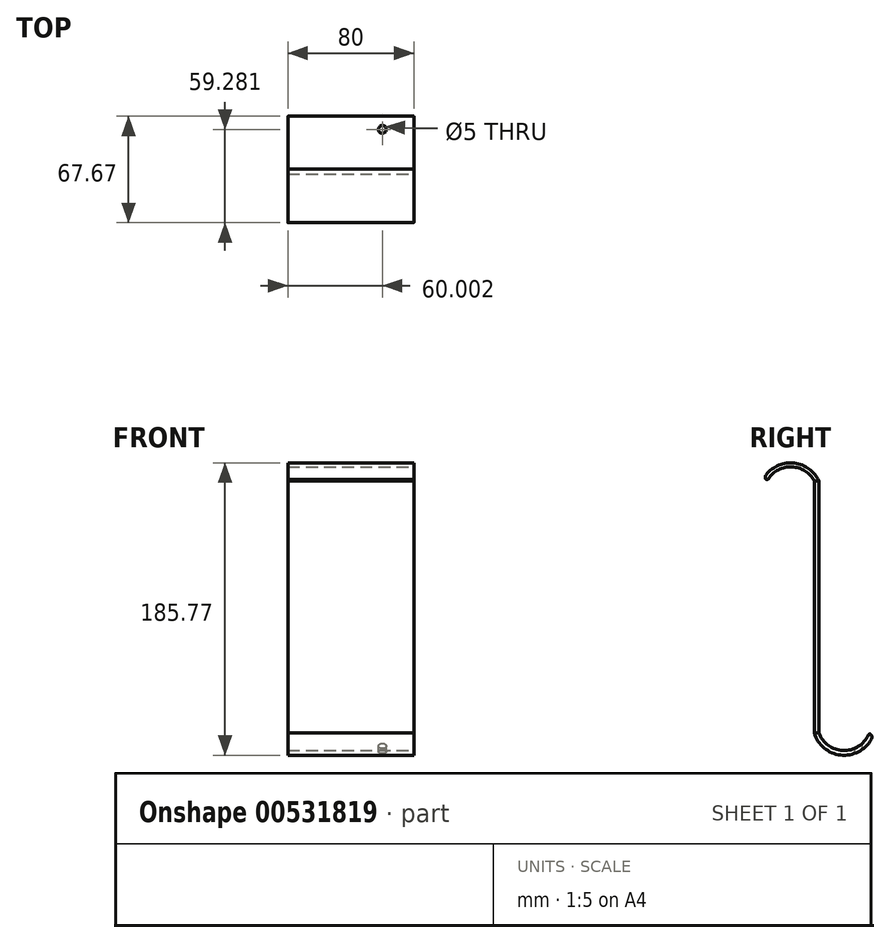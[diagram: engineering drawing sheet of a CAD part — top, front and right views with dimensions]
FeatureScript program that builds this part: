
annotation { "Feature Type Name" : "Feature", "Feature Type Description" : "" }
export const myFeature = defineFeature(function(context is Context, id is Id, definition is map)
    precondition{}
    {
        {
            var Q0;
            Q0=qCreatedBy(makeId("Front.planeOp"),FACE);
            var sketch = newSketch(context, id + "F0", { "sketchPlane" : qUnion([Q0])});
            skLineSegment(sketch, "E0", {"start": v(-47.36, 34.9) * mm, "end": v(32.64, 34.9) * mm});
            skLineSegment(sketch, "E1", {"start": v(-47.36, 34.9) * mm, "end": v(-47.36, -125.1) * mm});
            skLineSegment(sketch, "E2", {"start": v(-47.36, -125.1) * mm, "end": v(32.64, -125.1) * mm});
            skLineSegment(sketch, "E3", {"start": v(32.64, -125.1) * mm, "end": v(32.64, 34.9) * mm});
            skSolve(sketch);
        }
        {
            var Q0;
            Q0=makeQuery(id+"F0.imprint","IMPRINT",FACE,{"disambiguationData":[TD([[makeQuery(id+"F0.imprint","IMPRINT",EDGE,{"derivedFrom":sQuery(id+"F0.wireOp",EDGE,"E0")}),-1.0]])]});
            var Q1;
            Q1=sQuery(id+"F0.wireOp",EDGE,"E1");
            var Q2;
            Q2=sQuery(id+"F0.wireOp",EDGE,"E3");
            extrude(context, id + "F1", {"entities" : qUnion([Q0]), "surfaceEntities" : qUnion([Q1, Q2]), "depth" : 3 * mm, "offsetDistance" : 25 * mm});
        }
        {
            var Q0;
            Q0=makeQuery(id+"F1.opExtrude","SWEPT_FACE",FACE,{"disambiguationData":[OSD([sQuery(id+"F0.wireOp",EDGE,"E3")])]});
            var sketch = newSketch(context, id + "F2", { "sketchPlane" : qUnion([Q0])});
            skArc(sketch, "E4", {"start": v(0, 34.9) * mm, "mid": v(-18, 46.46) * mm, "end": v(-36, 34.9) * mm});
            skArc(sketch, "E5", {"start": v(-3, 34.9) * mm, "mid": v(-18, 43.9) * mm, "end": v(-33, 34.9) * mm});
            skLineSegment(sketch, "E6", {"start": v(-33, 34.9) * mm, "end": v(-36, 34.9) * mm});
            skArc(sketch, "E7", {"start": v(0, -125.1) * mm, "mid": v(15.98, -136.3) * mm, "end": v(31.96, -125.1) * mm});
            skArc(sketch, "E8", {"start": v(-3, -125.1) * mm, "mid": v(15.98, -139.3) * mm, "end": v(34.96, -125.1) * mm});
            skPoint(sketch, "E8.endSnap0", {"position": v(-1.5, -125.1) * mm});
            skLineSegment(sketch, "E9", {"start": v(31.96, -125.1) * mm, "end": v(34.96, -125.1) * mm});
            skSolve(sketch);
        }
        {
            var Q0;
            Q0=makeQuery(id+"F2.imprint","IMPRINT",FACE,{"disambiguationData":[TD([[makeQuery(id+"F2.imprint","IMPRINT",EDGE,{"derivedFrom":sQuery(id+"F2.wireOp",EDGE,"E4")}),1.0]])]});
            var Q1;
            Q1=makeQuery(id+"F2.imprint","IMPRINT",FACE,{"disambiguationData":[TD([[makeQuery(id+"F2.imprint","IMPRINT",EDGE,{"derivedFrom":sQuery(id+"F2.wireOp",EDGE,"E7")}),-1.0]])]});
            extrude(context, id + "F3", {"entities" : qUnion([Q0, Q1]), "oppositeDirection" : true, "depth" : 80 * mm, "offsetDistance" : 25 * mm});
        }
        {
            var Q0;
            Q0=makeQuery(id+"F3.opExtrude","SWEPT_EDGE",EDGE,{"disambiguationData":[OSD([sQuery(id+"F2.wireOp",EDGE,"E8"),sQuery(id+"F2.wireOp",EDGE,"E9")])]});
            var Q1;
            Q1=makeQuery(id+"F3.opExtrude","SWEPT_EDGE",EDGE,{"disambiguationData":[OSD([sQuery(id+"F2.wireOp",EDGE,"E4"),sQuery(id+"F2.wireOp",EDGE,"E6")])]});
            fillet(context, id + "F4", {"entities" : qUnion([Q0, Q1]), "radius" : 3 * mm, "tangentPropagation" : true, "allowEdgeOverflow" : false});
        }
        {
            var Q0;
            Q0=makeQuery(id+"F4.opFillet","BLEND_EDGE",EDGE,{"blendedFrom":[makeQuery(id+"F3.opExtrude","SWEPT_EDGE",EDGE,{"disambiguationData":[OSD([sQuery(id+"F2.wireOp",EDGE,"E8"),sQuery(id+"F2.wireOp",EDGE,"E9")])]}),makeQuery(id+"F3.opExtrude","SWEPT_FACE",FACE,{"disambiguationData":[OSD([sQuery(id+"F2.wireOp",EDGE,"E7")])]})],"blendedInto":[makeQuery(id+"F3.opExtrude","SWEPT_FACE",FACE,{"disambiguationData":[OSD([sQuery(id+"F2.wireOp",EDGE,"E7")])]})]});
            var Q1;
            Q1=makeQuery(id+"F4.opFillet","BLEND_EDGE",EDGE,{"blendedFrom":[makeQuery(id+"F3.opExtrude","SWEPT_EDGE",EDGE,{"disambiguationData":[OSD([sQuery(id+"F2.wireOp",EDGE,"E4"),sQuery(id+"F2.wireOp",EDGE,"E6")])]}),makeQuery(id+"F3.opExtrude","SWEPT_FACE",FACE,{"disambiguationData":[OSD([sQuery(id+"F2.wireOp",EDGE,"E5")])]})],"blendedInto":[makeQuery(id+"F3.opExtrude","SWEPT_FACE",FACE,{"disambiguationData":[OSD([sQuery(id+"F2.wireOp",EDGE,"E5")])]})]});
            fillet(context, id + "F5", {"entities" : qUnion([Q0, Q1]), "radius" : 1 * mm, "tangentPropagation" : true, "allowEdgeOverflow" : false});
        }
        {
            var Q0;
            Q0=qCreatedBy(makeId("Top.planeOp"),FACE);
            var sketch = newSketch(context, id + "F6", { "sketchPlane" : qUnion([Q0])});
            skCircle(sketch, "E10", {"center": v(12.64, 25.21) * mm, "radius": 2.5 * mm});
            skSolve(sketch);
        }
        {
            var Q0;
            Q0 = qSketchRegion(id + "F6", true);
            extrude(context, id + "F7", {"entities" : qUnion([Q0]), "operationType" : NewBodyOperationType.REMOVE, "endBound" : BoundingType.THROUGH_ALL, "oppositeDirection" : true, "depth" : 25 * mm, "offsetDistance" : 25 * mm});
        }
    });
